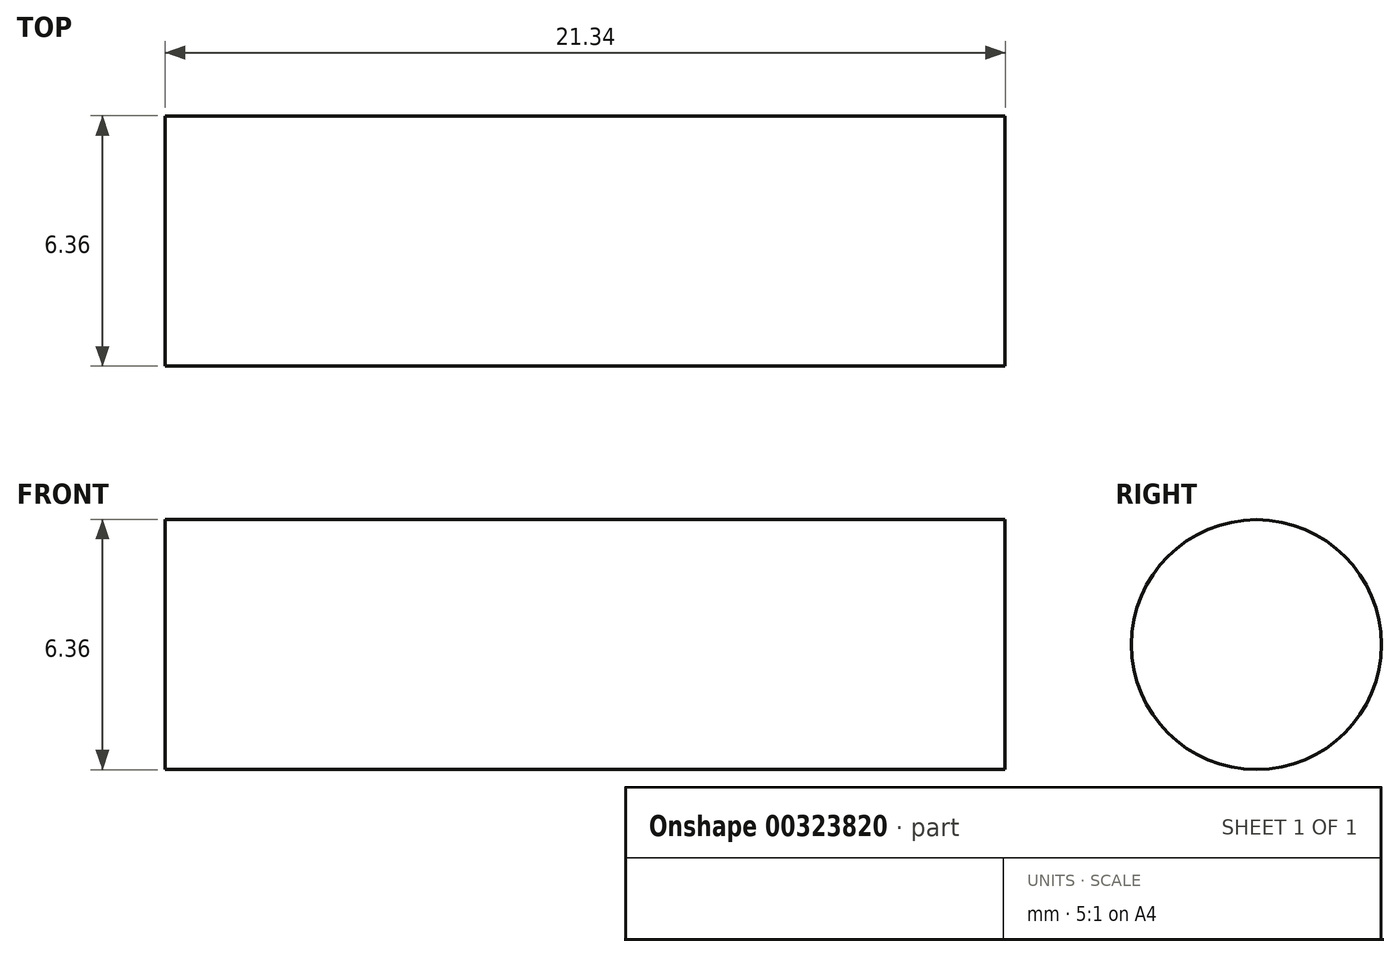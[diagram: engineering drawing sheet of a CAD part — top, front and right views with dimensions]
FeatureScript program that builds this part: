
annotation { "Feature Type Name" : "Feature", "Feature Type Description" : "" }
export const myFeature = defineFeature(function(context is Context, id is Id, definition is map)
    precondition{}
    {
        {
            var Q0;
            Q0=qCreatedBy(makeId("Right.planeOp"),FACE);
            var sketch = newSketch(context, id + "F0", { "sketchPlane" : qUnion([Q0])});
            skCircle(sketch, "E0", {"center": v(0, 0) * mm, "radius": 3.18 * mm});
            skSolve(sketch);
        }
        {
            var Q0;
            Q0=makeQuery(id+"F0.imprint","IMPRINT",FACE,{"disambiguationData":[TD([[makeQuery(id+"F0.imprint","IMPRINT",EDGE,{"derivedFrom":sQuery(id+"F0.wireOp",EDGE,"E0")}),1.0]])]});
            extrude(context, id + "F1", {"entities" : qUnion([Q0]), "depth" : 21.34 * mm});
        }
    });
